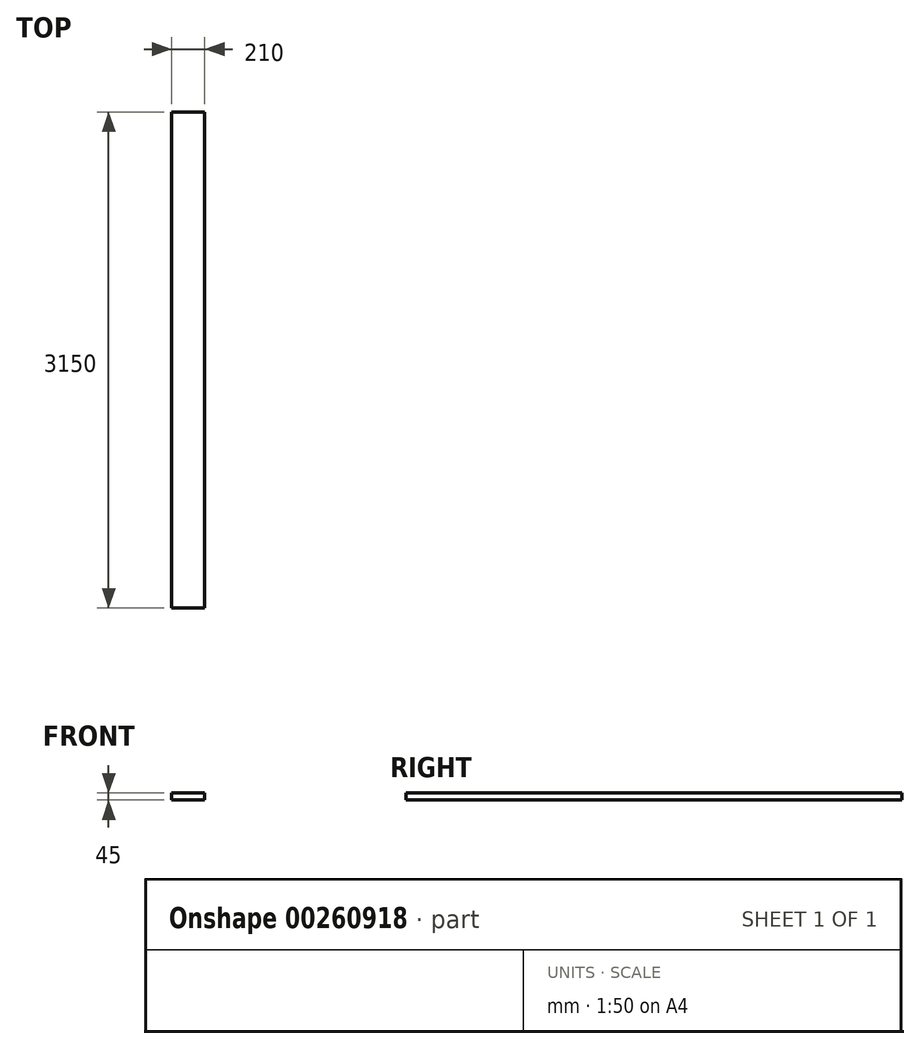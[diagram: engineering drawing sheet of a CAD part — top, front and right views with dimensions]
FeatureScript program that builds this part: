
annotation { "Feature Type Name" : "Feature", "Feature Type Description" : "" }
export const myFeature = defineFeature(function(context is Context, id is Id, definition is map)
    precondition{}
    {
        {
            var Q0;
            Q0=qCreatedBy(makeId("Front.planeOp"),FACE);
            var sketch = newSketch(context, id + "F0", { "sketchPlane" : qUnion([Q0])});
            skLineSegment(sketch, "E0.bottom", {"start": v(0, 0) * mm, "end": v(210, 0) * mm});
            skLineSegment(sketch, "E0.top", {"start": v(0, 45) * mm, "end": v(210, 45) * mm});
            skLineSegment(sketch, "E0.left", {"start": v(0, 0) * mm, "end": v(0, 45) * mm});
            skLineSegment(sketch, "E0.right", {"start": v(210, 0) * mm, "end": v(210, 45) * mm});
            skSolve(sketch);
        }
        {
            var Q0;
            Q0=makeQuery(id+"F0.imprint","IMPRINT",FACE,{"disambiguationData":[TD([[makeQuery(id+"F0.imprint","IMPRINT",EDGE,{"derivedFrom":sQuery(id+"F0.wireOp",EDGE,"E0.bottom")}),1.0]])]});
            extrude(context, id + "F1", {"entities" : qUnion([Q0]), "depth" : 3150 * mm});
        }
    });
